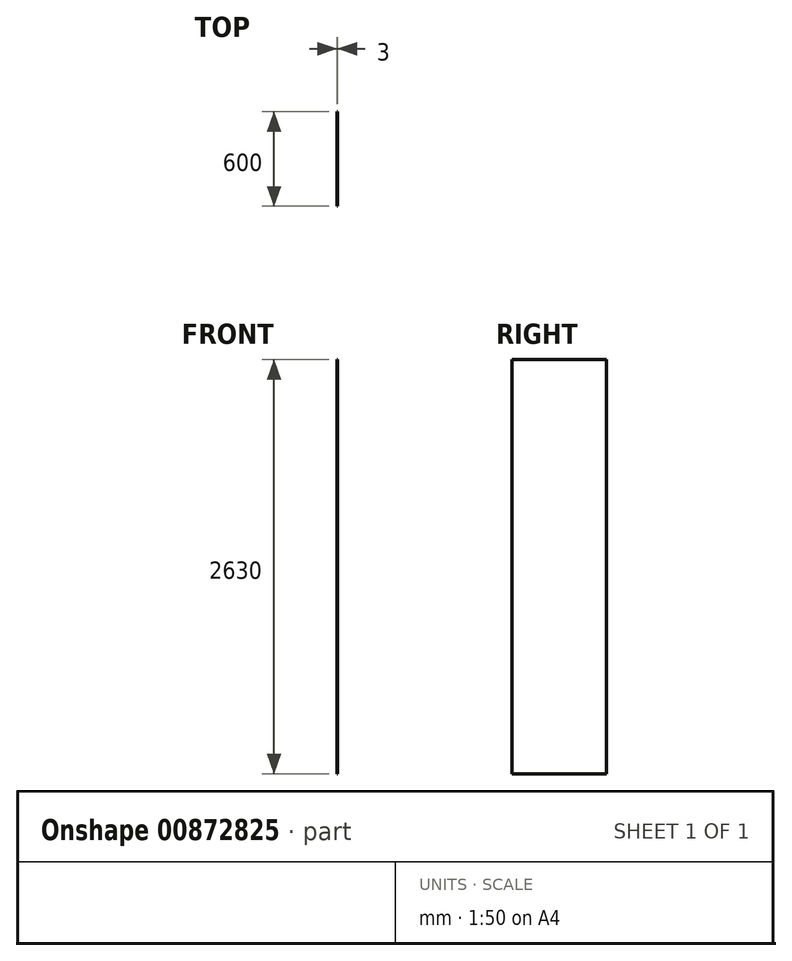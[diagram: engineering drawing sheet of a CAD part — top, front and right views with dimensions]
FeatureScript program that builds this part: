
annotation { "Feature Type Name" : "Feature", "Feature Type Description" : "" }
export const myFeature = defineFeature(function(context is Context, id is Id, definition is map)
    precondition{}
    {
        {
            var Q0;
            Q0=qCreatedBy(makeId("Right.planeOp"),FACE);
            var sketch = newSketch(context, id + "F0", { "sketchPlane" : qUnion([Q0])});
            skLineSegment(sketch, "E0.bottom", {"start": v(-300, 1315) * mm, "end": v(300, 1315) * mm});
            skLineSegment(sketch, "E0.top", {"start": v(-300, -1315) * mm, "end": v(300, -1315) * mm});
            skLineSegment(sketch, "E0.left", {"start": v(-300, 1315) * mm, "end": v(-300, -1315) * mm});
            skLineSegment(sketch, "E0.right", {"start": v(300, 1315) * mm, "end": v(300, -1315) * mm});
            skPoint(sketch, "E0.middle", {"position": v(0, 0) * mm});
            skSolve(sketch);
        }
        {
            var Q0;
            Q0 = qSketchRegion(id + "F0", true);
            extrude(context, id + "F1", {"entities" : qUnion([Q0]), "depth" : 3 * mm, "offsetDistance" : 25 * mm});
        }
    });
